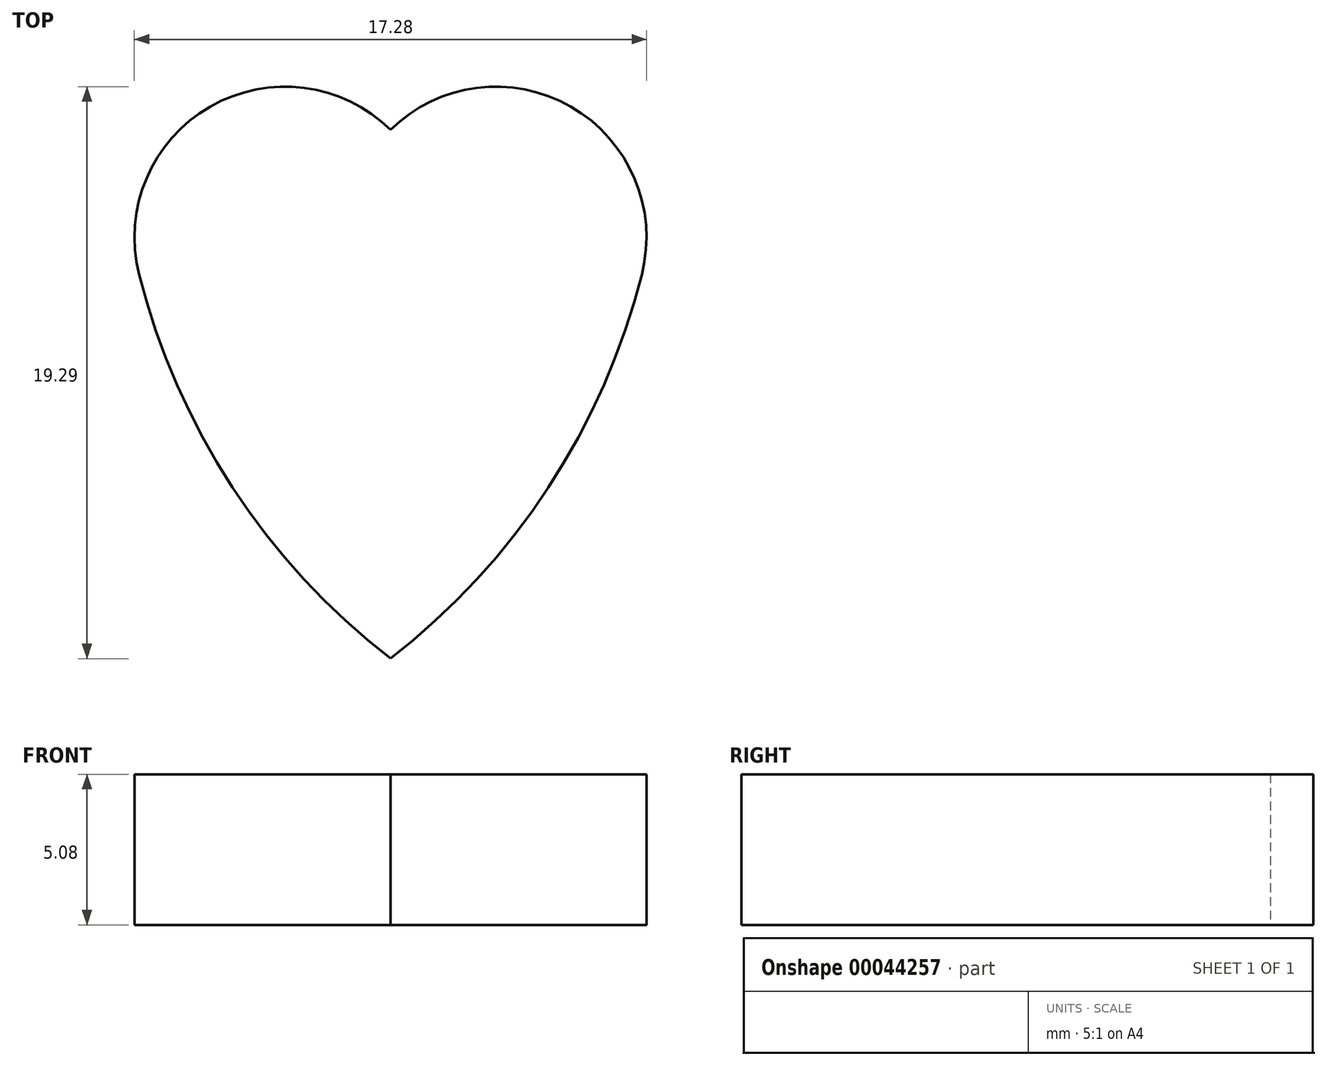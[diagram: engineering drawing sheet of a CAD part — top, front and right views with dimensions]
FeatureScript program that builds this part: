
annotation { "Feature Type Name" : "Feature", "Feature Type Description" : "" }
export const myFeature = defineFeature(function(context is Context, id is Id, definition is map)
    precondition{}
    {
        {
            var Q0;
            Q0=qCreatedBy(makeId("Top.planeOp"),FACE);
            var sketch = newSketch(context, id + "F0", { "sketchPlane" : qUnion([Q0])});
            skArc(sketch, "E0", {"start": v(0, 0.9) * mm, "mid": v(-6.09, 1.68) * mm, "end": v(-8.48, -3.96) * mm});
            skArc(sketch, "E1", {"start": v(-8.48, -3.96) * mm, "mid": v(-5.33, -11.16) * mm, "end": v(0, -16.93) * mm});
            skPoint(sketch, "E2.orphan", {"position": v(0, 0) * mm});
            skPoint(sketch, "E3.end.orphan", {"position": v(0, -33.85) * mm});
            skArc(sketch, "E4.MirrorCS", {"start": v(0, 0.9) * mm, "mid": v(6.09, 1.68) * mm, "end": v(8.48, -3.96) * mm});
            skArc(sketch, "E5.MirrorCS", {"start": v(8.48, -3.96) * mm, "mid": v(5.33, -11.16) * mm, "end": v(0, -16.93) * mm});
            skSolve(sketch);
        }
        {
            var Q0;
            Q0=makeQuery(id+"F0.imprint","IMPRINT",FACE,{"disambiguationData":[TD([[makeQuery(id+"F0.imprint","IMPRINT",EDGE,{"derivedFrom":sQuery(id+"F0.wireOp",EDGE,"E0")}),1.0]])]});
            extrude(context, id + "F1", {"entities" : qUnion([Q0]), "depth" : 5.08 * mm});
        }
    });
